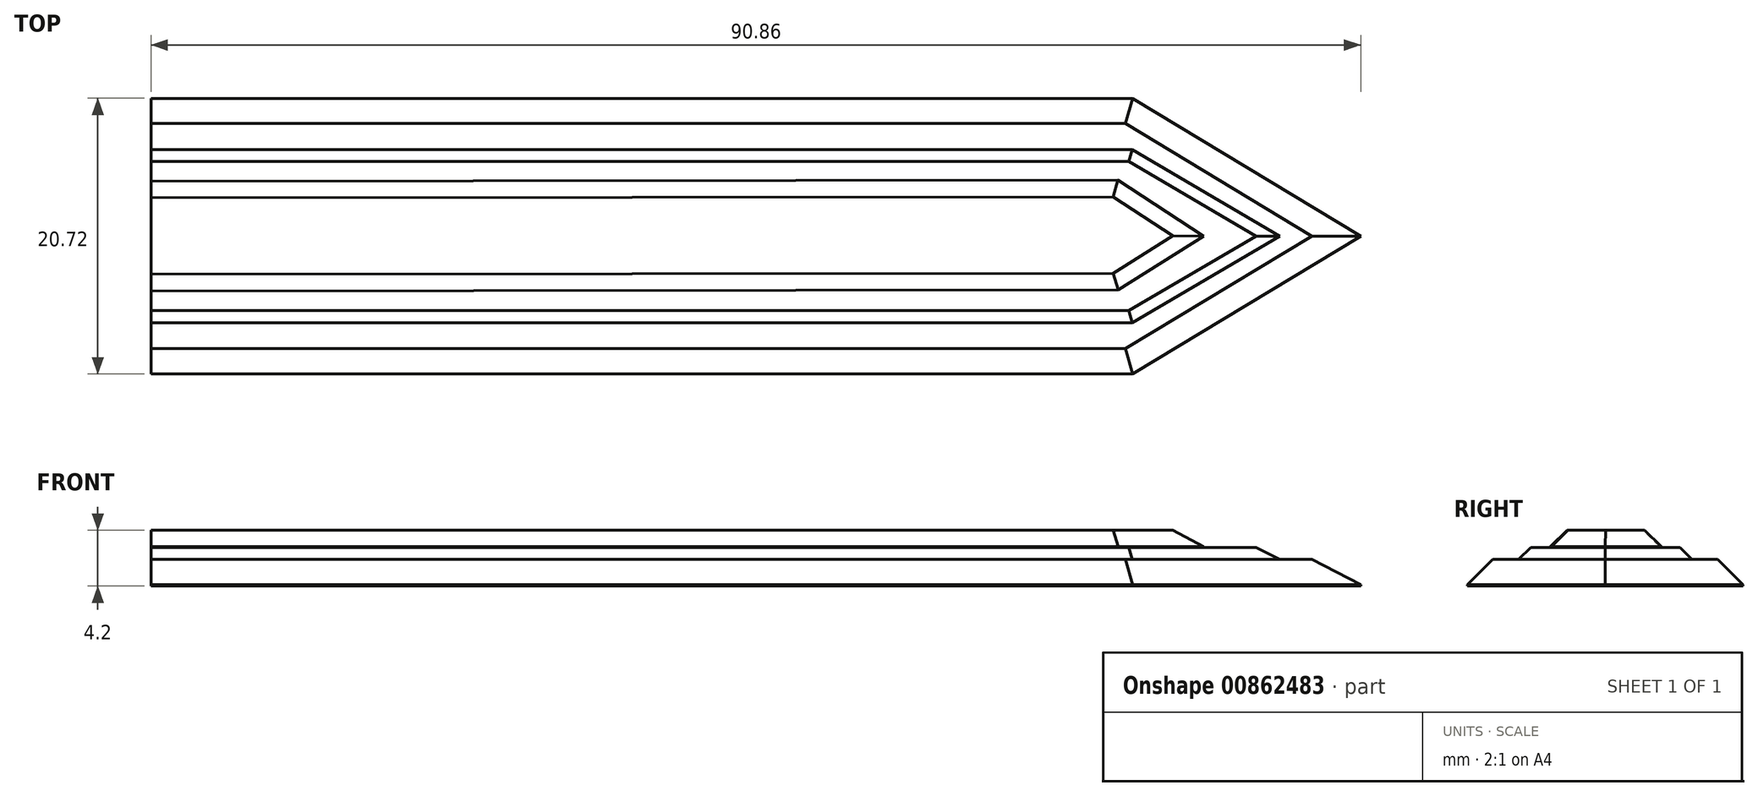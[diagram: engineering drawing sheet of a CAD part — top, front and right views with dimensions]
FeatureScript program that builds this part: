
annotation { "Feature Type Name" : "Feature", "Feature Type Description" : "" }
export const myFeature = defineFeature(function(context is Context, id is Id, definition is map)
    precondition{}
    {
        {
            var Q0;
            Q0=qCreatedBy(makeId("Top.planeOp"),FACE);
            var sketch = newSketch(context, id + "F0", { "sketchPlane" : qUnion([Q0])});
            skLineSegment(sketch, "E0.bottom", {"start": v(36.58, -10.36) * mm, "end": v(-36.86, -10.36) * mm});
            skLineSegment(sketch, "E0.top", {"start": v(36.58, 10.36) * mm, "end": v(-36.86, 10.36) * mm});
            skLineSegment(sketch, "E0.left", {"start": v(36.86, -10.36) * mm, "end": v(36.86, 10.36) * mm});
            skLineSegment(sketch, "E0.right", {"start": v(-36.86, -10.36) * mm, "end": v(-36.86, 10.36) * mm});
            skPoint(sketch, "E0.middle", {"position": v(0, 0) * mm});
            skLineSegment(sketch, "E1", {"start": v(36.86, 0) * mm, "end": v(54, 0) * mm});
            skLineSegment(sketch, "E2", {"start": v(54, 0) * mm, "end": v(37.1, 10.21) * mm});
            skLineSegment(sketch, "E3", {"start": v(37.1, -10.21) * mm, "end": v(54, 0) * mm});
            skPoint(sketch, "E4.visualSharp", {"position": v(36.86, 10.36) * mm});
            skPoint(sketch, "E5.startSnap0", {"position": v(45.55, 5.1) * mm});
            skPoint(sketch, "E5.endSnap0", {"position": v(45.55, 5.1) * mm});
            skLineSegment(sketch, "E6.0", {"start": v(35.76, 4.2) * mm, "end": v(-36.86, 4.13) * mm});
            skLineSegment(sketch, "E6.1", {"start": v(42.2, 0) * mm, "end": v(35.76, 4.2) * mm});
            skLineSegment(sketch, "E6.2", {"start": v(35.77, -4.05) * mm, "end": v(42.2, 0) * mm});
            skLineSegment(sketch, "E6.3", {"start": v(35.77, -4.05) * mm, "end": v(-36.86, -4.12) * mm});
            skLineSegment(sketch, "E7.0", {"start": v(36.85, 6.6) * mm, "end": v(-36.86, 6.6) * mm});
            skLineSegment(sketch, "E7.1", {"start": v(48.1, 0) * mm, "end": v(36.85, 6.6) * mm});
            skLineSegment(sketch, "E7.2", {"start": v(36.85, -6.6) * mm, "end": v(48.1, 0) * mm});
            skLineSegment(sketch, "E7.3", {"start": v(36.85, -6.6) * mm, "end": v(-36.86, -6.6) * mm});
            skLineSegment(sketch, "E8", {"start": v(37.1, 10.21) * mm, "end": v(36.86, 10.36) * mm});
            skLineSegment(sketch, "E9", {"start": v(36.58, 10.36) * mm, "end": v(36.86, 10.36) * mm});
            skLineSegment(sketch, "E10", {"start": v(37.1, -10.21) * mm, "end": v(36.86, -10.36) * mm});
            skLineSegment(sketch, "E11", {"start": v(36.58, -10.36) * mm, "end": v(36.86, -10.36) * mm});
            skSolve(sketch);
        }
        {
            var Q0;
            {var subQ1=sQuery(id+"F0.wireOp",EDGE,"E0.top");Q0=makeQuery(id+"F0.imprint","IMPRINT",FACE,{"disambiguationData":[TD([[makeQuery(id+"F0.imprint","IMPRINT",EDGE,{"derivedFrom":subQ1}),1.0]])]});}
            var Q1;
            {var subQ1=sQuery(id+"F0.wireOp",EDGE,"E0.bottom");Q1=makeQuery(id+"F0.imprint","IMPRINT",FACE,{"disambiguationData":[TD([[makeQuery(id+"F0.imprint","IMPRINT",EDGE,{"derivedFrom":subQ1}),-1.0]])]});}
            var Q2;
            {var subQ1=sQuery(id+"F0.wireOp",EDGE,"E2");Q2=makeQuery(id+"F0.imprint","IMPRINT",FACE,{"disambiguationData":[TD([[makeQuery(id+"F0.imprint","IMPRINT",EDGE,{"derivedFrom":subQ1}),1.0]])]});}
            var Q3;
            {var subQ1=sQuery(id+"F0.wireOp",EDGE,"E3");Q3=makeQuery(id+"F0.imprint","IMPRINT",FACE,{"disambiguationData":[TD([[makeQuery(id+"F0.imprint","IMPRINT",EDGE,{"derivedFrom":subQ1}),1.0]])]});}
            extrude(context, id + "F1", {"entities" : qUnion([Q0, Q1, Q2, Q3]), "depth" : 2 * mm, "offsetDistance" : 25 * mm});
        }
        {
            var Q0;
            {var subQ0=sQuery(id+"F0.wireOp",EDGE,"E6.3");Q0=makeQuery(id+"F0.imprint","IMPRINT",FACE,{"disambiguationData":[TD([[makeQuery(id+"F0.imprint","IMPRINT",EDGE,{"derivedFrom":subQ0}),1.0]])]});}
            var Q1;
            {var subQ0=sQuery(id+"F0.wireOp",EDGE,"E7.2");Q1=makeQuery(id+"F0.imprint","IMPRINT",FACE,{"disambiguationData":[TD([[makeQuery(id+"F0.imprint","IMPRINT",EDGE,{"derivedFrom":subQ0}),1.0]])]});}
            var Q2;
            {var subQ1=sQuery(id+"F0.wireOp",EDGE,"E6.0");Q2=makeQuery(id+"F0.imprint","IMPRINT",FACE,{"disambiguationData":[TD([[makeQuery(id+"F0.imprint","IMPRINT",EDGE,{"derivedFrom":subQ1}),-1.0]])]});}
            var Q3;
            {var subQ0=sQuery(id+"F0.wireOp",EDGE,"E7.1");Q3=makeQuery(id+"F0.imprint","IMPRINT",FACE,{"disambiguationData":[TD([[makeQuery(id+"F0.imprint","IMPRINT",EDGE,{"derivedFrom":subQ0}),1.0]])]});}
            extrude(context, id + "F2", {"entities" : qUnion([Q0, Q1, Q2, Q3]), "operationType" : NewBodyOperationType.ADD, "depth" : 2.9 * mm, "offsetDistance" : 25 * mm});
        }
        {
            var Q0;
            {var subQ0=sQuery(id+"F0.wireOp",EDGE,"E6.0");Q0=makeQuery(id+"F0.imprint","IMPRINT",FACE,{"disambiguationData":[TD([[makeQuery(id+"F0.imprint","IMPRINT",EDGE,{"derivedFrom":subQ0}),1.0]])]});}
            var Q1;
            {var subQ0=sQuery(id+"F0.wireOp",EDGE,"E1");var subQ1=sQuery(id+"F0.wireOp",EDGE,"E0.left");var subQ2=makeQuery(id+"F0.imprint","INTERSECT",VERTEX,{"derivedFrom":[subQ1,subQ0]});Q1=makeQuery(id+"F0.imprint","IMPRINT",FACE,{"disambiguationData":[TD([[makeQuery(id+"F0.imprint","IMPRINT",EDGE,{"disambiguationData":[TD([[subQ2,1.0]])],"derivedFrom":subQ1}),-1.0]])]});}
            var Q2;
            {var subQ0=sQuery(id+"F0.wireOp",EDGE,"E1");var subQ1=sQuery(id+"F0.wireOp",EDGE,"E0.left");var subQ2=makeQuery(id+"F0.imprint","INTERSECT",VERTEX,{"derivedFrom":[subQ1,subQ0]});Q2=makeQuery(id+"F0.imprint","IMPRINT",FACE,{"disambiguationData":[TD([[makeQuery(id+"F0.imprint","IMPRINT",EDGE,{"disambiguationData":[TD([[subQ2,-1.0]])],"derivedFrom":subQ1}),-1.0]])]});}
            extrude(context, id + "F3", {"entities" : qUnion([Q0, Q1, Q2]), "operationType" : NewBodyOperationType.ADD, "depth" : 4.2 * mm, "offsetDistance" : 25 * mm});
        }
        {
            var Q0;
            Q0=makeQuery(id+"F3.opExtrude","CAP_EDGE",EDGE,{"disambiguationData":[OSD([sQuery(id+"F0.wireOp",EDGE,"E6.2")])],"isStart":false});
            var Q1;
            Q1=makeQuery(id+"F3.opExtrude","CAP_EDGE",EDGE,{"disambiguationData":[OSD([sQuery(id+"F0.wireOp",EDGE,"E6.3")])],"isStart":false});
            var Q2;
            Q2=makeQuery(id+"F3.opExtrude","CAP_EDGE",EDGE,{"disambiguationData":[OSD([sQuery(id+"F0.wireOp",EDGE,"E6.1")])],"isStart":false});
            var Q3;
            Q3=makeQuery(id+"F3.opExtrude","CAP_EDGE",EDGE,{"disambiguationData":[OSD([sQuery(id+"F0.wireOp",EDGE,"E6.0")])],"isStart":false});
            chamfer(context, id + "F4", {"entities" : qUnion([Q0, Q1, Q2, Q3]), "width" : 1.25 * mm, "tangentPropagation" : true});
        }
        {
            var Q0;
            Q0=makeQuery(id+"F2.opExtrude","CAP_EDGE",EDGE,{"disambiguationData":[OSD([sQuery(id+"F0.wireOp",EDGE,"E7.1")])],"isStart":false});
            var Q1;
            Q1=makeQuery(id+"F2.opExtrude","CAP_EDGE",EDGE,{"disambiguationData":[OSD([sQuery(id+"F0.wireOp",EDGE,"E7.2")])],"isStart":false});
            var Q2;
            Q2=makeQuery(id+"F2.opExtrude","CAP_EDGE",EDGE,{"disambiguationData":[OSD([sQuery(id+"F0.wireOp",EDGE,"E7.3")])],"isStart":false});
            var Q3;
            Q3=makeQuery(id+"F2.opExtrude","CAP_EDGE",EDGE,{"disambiguationData":[OSD([sQuery(id+"F0.wireOp",EDGE,"E7.0")])],"isStart":false});
            chamfer(context, id + "F5", {"entities" : qUnion([Q0, Q1, Q2, Q3]), "width" : 1 * mm, "tangentPropagation" : true});
        }
        {
            var Q0;
            Q0=makeQuery(id+"F1.opExtrude","CAP_EDGE",EDGE,{"disambiguationData":[OSD([sQuery(id+"F0.wireOp",EDGE,"E2"),sQuery(id+"F0.wireOp",EDGE,"E8")])],"isStart":false});
            var Q1;
            Q1=makeQuery(id+"F1.opExtrude","CAP_EDGE",EDGE,{"disambiguationData":[OSD([sQuery(id+"F0.wireOp",EDGE,"E0.top"),sQuery(id+"F0.wireOp",EDGE,"E9")])],"isStart":false});
            var Q2;
            Q2=makeQuery(id+"F1.opExtrude","CAP_EDGE",EDGE,{"disambiguationData":[OSD([sQuery(id+"F0.wireOp",EDGE,"E0.bottom"),sQuery(id+"F0.wireOp",EDGE,"E11")])],"isStart":false});
            var Q3;
            Q3=makeQuery(id+"F1.opExtrude","CAP_EDGE",EDGE,{"disambiguationData":[OSD([sQuery(id+"F0.wireOp",EDGE,"E3"),sQuery(id+"F0.wireOp",EDGE,"E10")])],"isStart":false});
            chamfer(context, id + "F6", {"entities" : qUnion([Q0, Q1, Q2, Q3]), "width" : 1.9 * mm, "tangentPropagation" : true});
        }
    });
